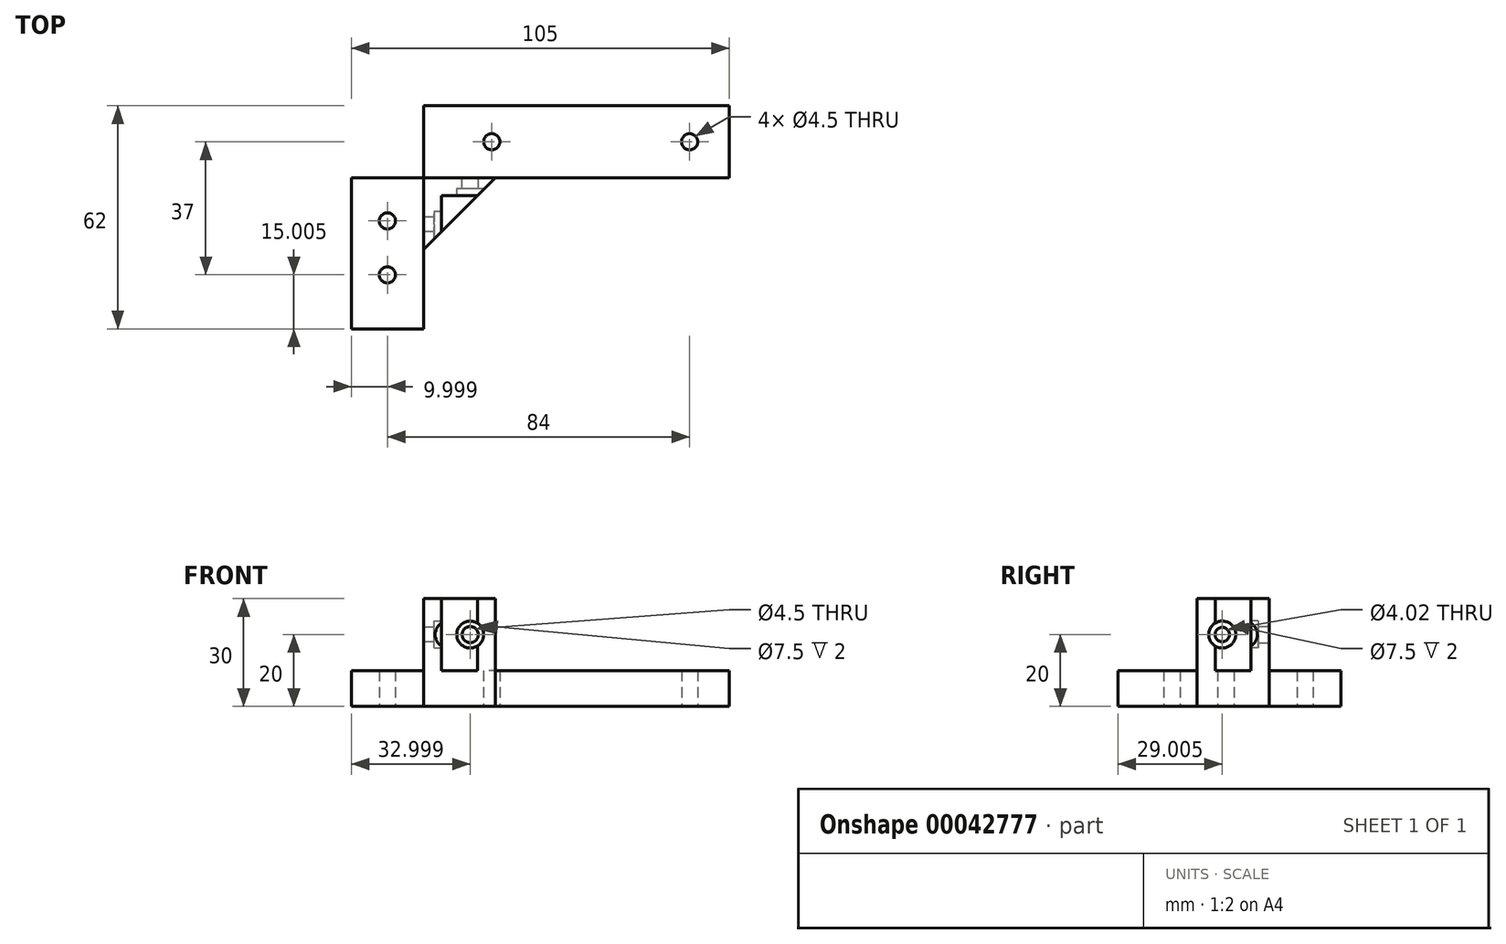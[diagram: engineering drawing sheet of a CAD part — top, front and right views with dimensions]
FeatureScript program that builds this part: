
annotation { "Feature Type Name" : "Feature", "Feature Type Description" : "" }
export const myFeature = defineFeature(function(context is Context, id is Id, definition is map)
    precondition{}
    {
        {
            var Q0;
            Q0=qCreatedBy(makeId("Top.planeOp"),FACE);
            var sketch = newSketch(context, id + "F0", { "sketchPlane" : qUnion([Q0])});
            skLineSegment(sketch, "E0", {"start": v(15.56, -35.74) * mm, "end": v(35.56, -35.74) * mm});
            skLineSegment(sketch, "E1", {"start": v(35.56, 6.26) * mm, "end": v(15.56, 6.26) * mm});
            skLineSegment(sketch, "E2", {"start": v(25.56, 6.26) * mm, "end": v(25.56, -5.74) * mm, "construction": true});
            skCircle(sketch, "E3", {"center": v(25.56, -5.74) * mm, "radius": 2.25 * mm});
            skLineSegment(sketch, "E4", {"start": v(25.56, -5.74) * mm, "end": v(25.56, -20.74) * mm, "construction": true});
            skCircle(sketch, "E5", {"center": v(25.56, -20.74) * mm, "radius": 2.25 * mm});
            skLineSegment(sketch, "E6", {"start": v(35.56, 6.26) * mm, "end": v(35.56, 26.26) * mm});
            skLineSegment(sketch, "E7", {"start": v(35.56, 26.26) * mm, "end": v(120.56, 26.26) * mm});
            skLineSegment(sketch, "E8", {"start": v(120.56, 26.26) * mm, "end": v(120.56, 6.26) * mm});
            skLineSegment(sketch, "E9", {"start": v(120.56, 6.26) * mm, "end": v(55.56, 6.26) * mm});
            skLineSegment(sketch, "E10", {"start": v(55.56, 6.26) * mm, "end": v(35.56, -13.74) * mm});
            skCircle(sketch, "E11", {"center": v(54.56, 16.26) * mm, "radius": 2.25 * mm});
            skLineSegment(sketch, "E12", {"start": v(54.56, 16.26) * mm, "end": v(109.56, 16.26) * mm, "construction": true});
            skCircle(sketch, "E13", {"center": v(109.56, 16.26) * mm, "radius": 2.25 * mm});
            skLineSegment(sketch, "E14", {"start": v(15.56, 6.26) * mm, "end": v(15.56, -35.74) * mm});
            skLineSegment(sketch, "E15", {"start": v(35.56, -35.74) * mm, "end": v(35.56, -13.74) * mm});
            skSolve(sketch);
        }
        {
            var Q0;
            Q0 = qSketchRegion(id + "F0", true);
            extrude(context, id + "F1", {"entities" : qUnion([Q0]), "depth" : 10 * mm});
        }
        {
            var Q0;
            Q0=makeQuery(id+"F1.opExtrude","CAP_FACE",FACE,{"disambiguationData":[OSD([sQuery(id+"F0.wireOp",EDGE,"E0"),sQuery(id+"F0.wireOp",EDGE,"E1"),sQuery(id+"F0.wireOp",EDGE,"E3"),sQuery(id+"F0.wireOp",EDGE,"E5"),sQuery(id+"F0.wireOp",EDGE,"E6"),sQuery(id+"F0.wireOp",EDGE,"E7"),sQuery(id+"F0.wireOp",EDGE,"E8"),sQuery(id+"F0.wireOp",EDGE,"E9"),sQuery(id+"F0.wireOp",EDGE,"E10"),sQuery(id+"F0.wireOp",EDGE,"E11"),sQuery(id+"F0.wireOp",EDGE,"E13"),sQuery(id+"F0.wireOp",EDGE,"E14"),sQuery(id+"F0.wireOp",EDGE,"E15")])],"isStart":false});
            var sketch = newSketch(context, id + "F2", { "sketchPlane" : qUnion([Q0])});
            skLineSegment(sketch, "E16", {"start": v(35.56, 6.26) * mm, "end": v(35.56, -13.74) * mm});
            skLineSegment(sketch, "E17", {"start": v(35.56, 6.26) * mm, "end": v(55.56, 6.26) * mm});
            skLineSegment(sketch, "E18", {"start": v(45.56, 6.26) * mm, "end": v(45.56, 1.26) * mm, "construction": true});
            skLineSegment(sketch, "E19", {"start": v(35.56, -3.74) * mm, "end": v(40.56, -3.74) * mm, "construction": true});
            skLineSegment(sketch, "E20", {"start": v(45.56, 1.26) * mm, "end": v(40.56, 1.26) * mm});
            skLineSegment(sketch, "E21", {"start": v(35.56, -13.74) * mm, "end": v(40.56, -8.74) * mm});
            skLineSegment(sketch, "E22", {"start": v(40.56, -8.74) * mm, "end": v(40.56, 1.26) * mm});
            skLineSegment(sketch, "E23", {"start": v(45.56, 1.26) * mm, "end": v(50.56, 1.26) * mm});
            skLineSegment(sketch, "E24", {"start": v(50.56, 1.26) * mm, "end": v(55.56, 6.26) * mm});
            skSolve(sketch);
        }
        {
            var Q0;
            Q0 = qSketchRegion(id + "F2", true);
            extrude(context, id + "F3", {"entities" : qUnion([Q0]), "operationType" : NewBodyOperationType.ADD, "depth" : 20 * mm});
        }
        {
            var Q0;
            Q0=makeQuery(id+"F3.opExtrude","SWEPT_FACE",FACE,{"disambiguationData":[OSD([sQuery(id+"F2.wireOp",EDGE,"E16")])]});
            var sketch = newSketch(context, id + "F4", { "sketchPlane" : qUnion([Q0])});
            skCircle(sketch, "E25", {"center": v(6.74, 20) * mm, "radius": 2 * mm});
            skSolve(sketch);
        }
        {
            var Q0;
            Q0 = qSketchRegion(id + "F4", true);
            extrude(context, id + "F5", {"entities" : qUnion([Q0]), "operationType" : NewBodyOperationType.REMOVE, "oppositeDirection" : true, "depth" : 5 * mm});
        }
        {
            var Q0;
            Q0=makeQuery(id+"F3.opExtrude","SWEPT_FACE",FACE,{"disambiguationData":[OSD([sQuery(id+"F2.wireOp",EDGE,"E17")])]});
            var sketch = newSketch(context, id + "F6", { "sketchPlane" : qUnion([Q0])});
            skPoint(sketch, "E26.centerSnap0", {"position": v(-48.56, 20) * mm});
            skCircle(sketch, "E27", {"center": v(-48.56, 20) * mm, "radius": 2.25 * mm});
            skSolve(sketch);
        }
        {
            var Q0;
            Q0 = qSketchRegion(id + "F6", true);
            extrude(context, id + "F7", {"entities" : qUnion([Q0]), "operationType" : NewBodyOperationType.REMOVE, "oppositeDirection" : true, "depth" : 5 * mm});
        }
        {
            var Q0;
            Q0=makeQuery(id+"F3.opExtrude","SWEPT_FACE",FACE,{"disambiguationData":[OSD([sQuery(id+"F2.wireOp",EDGE,"E20"),sQuery(id+"F2.wireOp",EDGE,"E23")])]});
            var sketch = newSketch(context, id + "F8", { "sketchPlane" : qUnion([Q0])});
            skCircle(sketch, "E28", {"center": v(48.56, 20) * mm, "radius": 3.75 * mm});
            skSolve(sketch);
        }
        {
            var Q0;
            Q0 = qSketchRegion(id + "F8", true);
            extrude(context, id + "F9", {"entities" : qUnion([Q0]), "operationType" : NewBodyOperationType.REMOVE, "oppositeDirection" : true, "depth" : 2 * mm});
        }
        {
            var Q0;
            Q0=makeQuery(id+"F3.opExtrude","SWEPT_FACE",FACE,{"disambiguationData":[OSD([sQuery(id+"F2.wireOp",EDGE,"E22")])]});
            var sketch = newSketch(context, id + "F10", { "sketchPlane" : qUnion([Q0])});
            skCircle(sketch, "E29", {"center": v(-6.74, 20) * mm, "radius": 3.75 * mm});
            skSolve(sketch);
        }
        {
            var Q0;
            Q0 = qSketchRegion(id + "F10", true);
            extrude(context, id + "F11", {"entities" : qUnion([Q0]), "operationType" : NewBodyOperationType.REMOVE, "oppositeDirection" : true, "depth" : 2 * mm});
        }
    });
